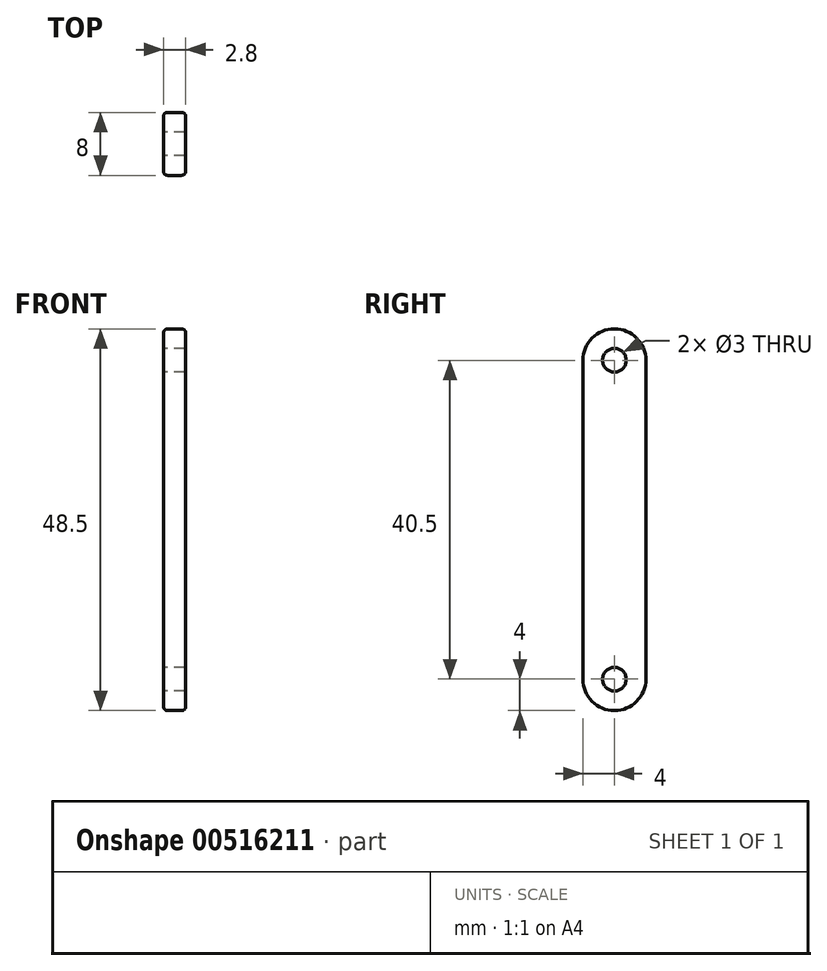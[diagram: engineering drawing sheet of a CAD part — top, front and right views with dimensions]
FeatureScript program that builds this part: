
annotation { "Feature Type Name" : "Feature", "Feature Type Description" : "" }
export const myFeature = defineFeature(function(context is Context, id is Id, definition is map)
    precondition{}
    {
        {
            var Q0;
            Q0=qCreatedBy(makeId("Top.planeOp"),FACE);
            var sketch = newSketch(context, id + "F0", { "sketchPlane" : qUnion([Q0])});
            skLineSegment(sketch, "E0.bottom", {"start": v(1.4, 4) * mm, "end": v(-1.4, 4) * mm});
            skLineSegment(sketch, "E0.top", {"start": v(1.4, -4) * mm, "end": v(-1.4, -4) * mm});
            skLineSegment(sketch, "E0.left", {"start": v(1.4, 4) * mm, "end": v(1.4, -4) * mm});
            skLineSegment(sketch, "E0.right", {"start": v(-1.4, 4) * mm, "end": v(-1.4, -4) * mm});
            skPoint(sketch, "E0.middle", {"position": v(0, 0) * mm});
            skSolve(sketch);
        }
        {
            var Q0;
            Q0=makeQuery(id+"F0.imprint","IMPRINT",FACE,{"disambiguationData":[TD([[makeQuery(id+"F0.imprint","IMPRINT",EDGE,{"derivedFrom":sQuery(id+"F0.wireOp",EDGE,"E0.bottom")}),1.0]])]});
            extrude(context, id + "F1", {"entities" : qUnion([Q0]), "depth" : 48.5 * mm, "offsetDistance" : 25 * mm});
        }
        {
            var Q0;
            Q0=makeQuery(id+"F1.opExtrude","CAP_EDGE",EDGE,{"disambiguationData":[OSD([sQuery(id+"F0.wireOp",EDGE,"E0.bottom")])],"isStart":true});
            var Q1;
            Q1=makeQuery(id+"F1.opExtrude","CAP_EDGE",EDGE,{"disambiguationData":[OSD([sQuery(id+"F0.wireOp",EDGE,"E0.top")])],"isStart":true});
            var Q2;
            Q2=makeQuery(id+"F1.opExtrude","CAP_EDGE",EDGE,{"disambiguationData":[OSD([sQuery(id+"F0.wireOp",EDGE,"E0.top")])],"isStart":false});
            var Q3;
            Q3=makeQuery(id+"F1.opExtrude","CAP_EDGE",EDGE,{"disambiguationData":[OSD([sQuery(id+"F0.wireOp",EDGE,"E0.bottom")])],"isStart":false});
            fillet(context, id + "F2", {"entities" : qUnion([Q0, Q1, Q2, Q3]), "radius" : 4 * mm, "tangentPropagation" : true, "allowEdgeOverflow" : false});
        }
        {
            var Q0;
            Q0=makeQuery(id+"F1.opExtrude","SWEPT_FACE",FACE,{"disambiguationData":[OSD([sQuery(id+"F0.wireOp",EDGE,"E0.right")])]});
            var sketch = newSketch(context, id + "F3", { "sketchPlane" : qUnion([Q0])});
            skCircle(sketch, "E1", {"center": v(0, 44.5) * mm, "radius": 1.5 * mm});
            skCircle(sketch, "E2", {"center": v(0, 4) * mm, "radius": 1.5 * mm});
            skSolve(sketch);
        }
        {
            var Q0;
            Q0=makeQuery(id+"F3.imprint","IMPRINT",FACE,{"disambiguationData":[TD([[makeQuery(id+"F3.imprint","IMPRINT",EDGE,{"derivedFrom":sQuery(id+"F3.wireOp",EDGE,"E2")}),1.0]])]});
            var Q1;
            Q1=makeQuery(id+"F3.imprint","IMPRINT",FACE,{"disambiguationData":[TD([[makeQuery(id+"F3.imprint","IMPRINT",EDGE,{"derivedFrom":sQuery(id+"F3.wireOp",EDGE,"E1")}),1.0]])]});
            extrude(context, id + "F4", {"entities" : qUnion([Q0, Q1]), "operationType" : NewBodyOperationType.REMOVE, "oppositeDirection" : true, "depth" : 5 * mm, "offsetDistance" : 25 * mm});
        }
        {
            var Q0;
            Q0=makeQuery(id+"F1.opExtrude","SWEPT_EDGE",EDGE,{"disambiguationData":[OSD([sQuery(id+"F0.wireOp",EDGE,"E0.bottom"),sQuery(id+"F0.wireOp",EDGE,"E0.right")])]});
            var Q1;
            Q1=makeQuery(id+"F1.opExtrude","SWEPT_EDGE",EDGE,{"disambiguationData":[OSD([sQuery(id+"F0.wireOp",EDGE,"E0.bottom"),sQuery(id+"F0.wireOp",EDGE,"E0.left")])]});
            fillet(context, id + "F5", {"entities" : qUnion([Q0, Q1]), "radius" : .5 * mm, "tangentPropagation" : true, "allowEdgeOverflow" : false});
        }
    });
